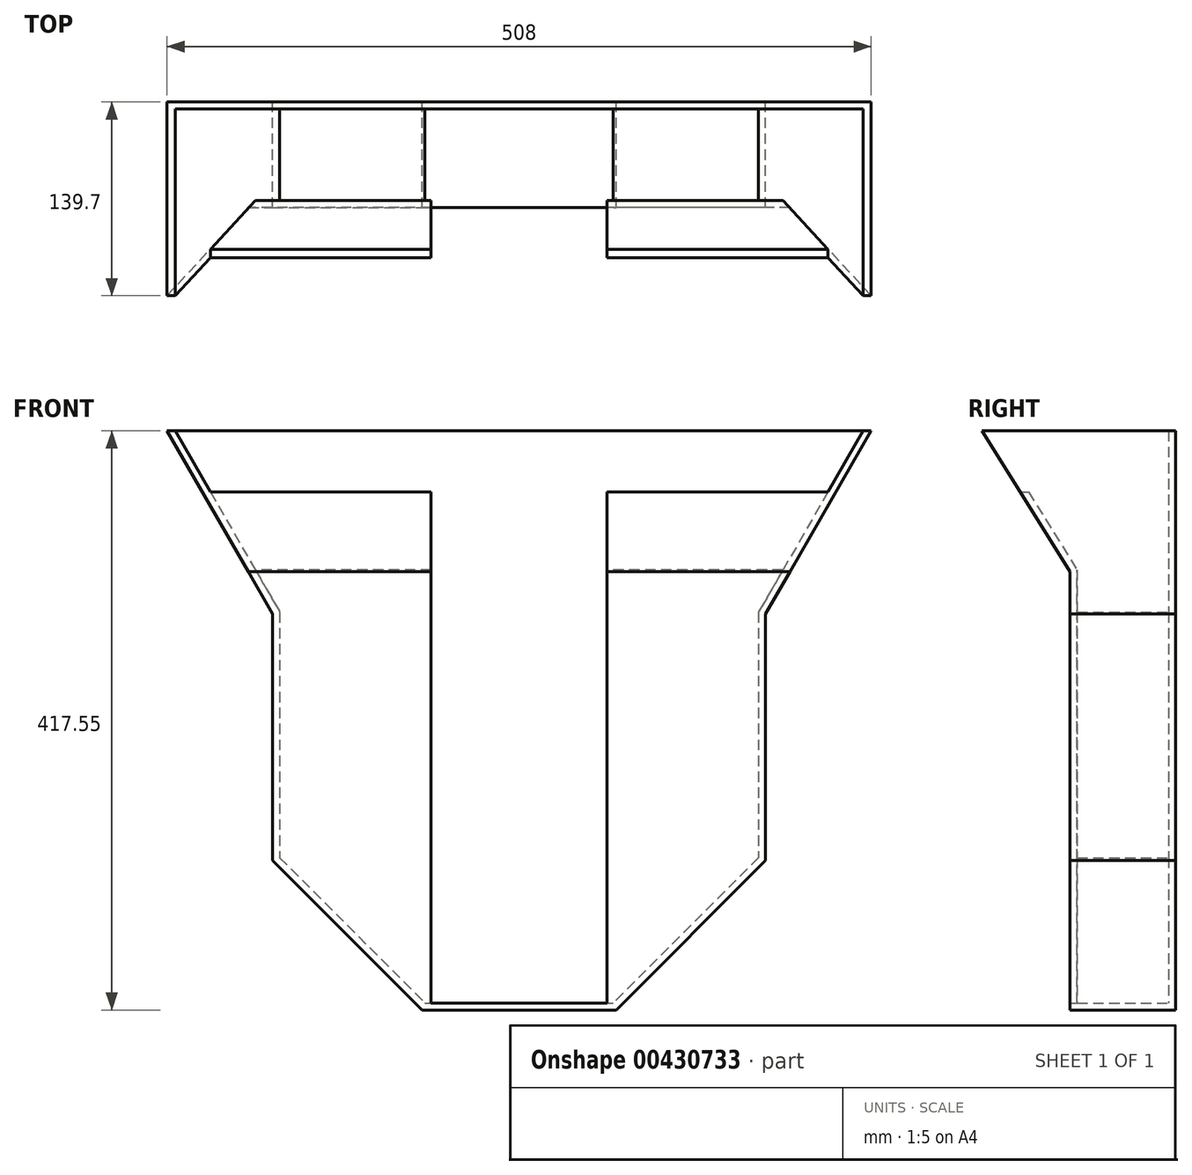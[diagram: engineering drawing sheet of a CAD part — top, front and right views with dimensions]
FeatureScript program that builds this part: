
annotation { "Feature Type Name" : "Feature", "Feature Type Description" : "" }
export const myFeature = defineFeature(function(context is Context, id is Id, definition is map)
    precondition{}
    {
        {
            var Q0;
            Q0=qCreatedBy(makeId("Front.planeOp"),FACE);
            var sketch = newSketch(context, id + "F0", { "sketchPlane" : qUnion([Q0])});
            skLineSegment(sketch, "E0", {"start": v(0, 0) * mm, "end": v(254, 0) * mm});
            skLineSegment(sketch, "E1", {"start": v(254, 0) * mm, "end": v(177.8, -131.98) * mm});
            skLineSegment(sketch, "E2", {"start": v(177.8, -131.98) * mm, "end": v(177.8, -309.78) * mm});
            skLineSegment(sketch, "E3", {"start": v(177.8, -309.78) * mm, "end": v(70.04, -417.55) * mm});
            skLineSegment(sketch, "E4", {"start": v(70.04, -417.55) * mm, "end": v(0, -417.55) * mm});
            skLineSegment(sketch, "E5.MirrorCS", {"start": v(0, 0) * mm, "end": v(-254, 0) * mm});
            skLineSegment(sketch, "E6.MirrorCS", {"start": v(-254, 0) * mm, "end": v(-177.8, -131.98) * mm});
            skLineSegment(sketch, "E7.MirrorCS", {"start": v(-177.8, -131.98) * mm, "end": v(-177.8, -309.78) * mm});
            skLineSegment(sketch, "E8.MirrorCS", {"start": v(-177.8, -309.78) * mm, "end": v(-70.04, -417.55) * mm});
            skLineSegment(sketch, "E9.MirrorCS", {"start": v(-70.04, -417.55) * mm, "end": v(0, -417.55) * mm});
            skSolve(sketch);
        }
        {
            var Q0;
            Q0=makeQuery(id+"F0.imprint","IMPRINT",FACE,{"disambiguationData":[TD([[makeQuery(id+"F0.imprint","IMPRINT",EDGE,{"derivedFrom":sQuery(id+"F0.wireOp",EDGE,"E0")}),-1.0]])]});
            extrude(context, id + "F1", {"entities" : qUnion([Q0]), "depth" : 76.2 * mm});
        }
        {
            var Q0;
            Q0=qCreatedBy(makeId("Right.planeOp"),FACE);
            var sketch = newSketch(context, id + "F2", { "sketchPlane" : qUnion([Q0])});
            skLineSegment(sketch, "E10", {"start": v(-76.2, 0) * mm, "end": v(-139.7, 0) * mm});
            skLineSegment(sketch, "E11", {"start": v(-139.7, 0) * mm, "end": v(-76.2, -101.6) * mm});
            skLineSegment(sketch, "E12", {"start": v(-76.2, -101.6) * mm, "end": v(-76.2, 0) * mm});
            skSolve(sketch);
        }
        {
            var Q0;
            Q0 = qSketchRegion(id + "F2", true);
            var Q1;
            Q1=makeQuery(id+"F1.opExtrude","SWEPT_FACE",FACE,{"disambiguationData":[OSD([sQuery(id+"F0.wireOp",EDGE,"E1")])]});
            var Q2;
            Q2=makeQuery(id+"F1.opExtrude","SWEPT_FACE",FACE,{"disambiguationData":[OSD([sQuery(id+"F0.wireOp",EDGE,"E6.MirrorCS")])]});
            extrude(context, id + "F3", {"entities" : qUnion([Q0]), "operationType" : NewBodyOperationType.ADD, "endBound" : BoundingType.UP_TO_SURFACE, "endBoundEntityFace" : qUnion([Q1]), "depth" : 25.4 * mm, "hasSecondDirection" : true, "secondDirectionBound" : BoundingType.UP_TO_SURFACE, "secondDirectionOppositeDirection" : true, "secondDirectionBoundEntityFace" : qUnion([Q2]), "secondDirectionDepth" : 25.4 * mm});
        }
        {
            var Q0;
            Q0=makeQuery(id+"F3.boolean.opBoolean","MERGE",FACE,{"derivedFrom":[makeQuery(id+"F1.opExtrude","SWEPT_FACE",FACE,{"disambiguationData":[OSD([sQuery(id+"F0.wireOp",EDGE,"E0"),sQuery(id+"F0.wireOp",EDGE,"E5.MirrorCS")])]}),makeQuery(id+"F3.opExtrude","SWEPT_FACE",FACE,{"disambiguationData":[OSD([sQuery(id+"F2.wireOp",EDGE,"E10")])]})]});
            shell(context, id + "F4", {"entities" : qUnion([Q0]), "thickness" : 5.08 * mm});
        }
        {
            var Q0;
            {var subQ0=sQuery(id+"F0.wireOp",EDGE,"E9.MirrorCS");var subQ1=sQuery(id+"F0.wireOp",EDGE,"E8.MirrorCS");var subQ2=sQuery(id+"F0.wireOp",EDGE,"E7.MirrorCS");var subQ3=sQuery(id+"F0.wireOp",EDGE,"E6.MirrorCS");var subQ4=sQuery(id+"F0.wireOp",EDGE,"E5.MirrorCS");var subQ5=sQuery(id+"F0.wireOp",EDGE,"E4");var subQ6=sQuery(id+"F0.wireOp",EDGE,"E3");var subQ7=sQuery(id+"F0.wireOp",EDGE,"E2");var subQ8=sQuery(id+"F0.wireOp",EDGE,"E1");var subQ9=sQuery(id+"F0.wireOp",EDGE,"E0");Q0=makeQuery(id+"F4.opShell","OFFSET_FACE",FACE,{"disambiguationData":[OSD([subQ9,subQ8,subQ7,subQ6,subQ5,subQ4,subQ3,subQ2,subQ1,subQ0]),TDD([makeQuery(id+"F1.opExtrude","CAP_FACE",FACE,{"disambiguationData":[OSD([subQ9,subQ8,subQ7,subQ6,subQ5,subQ4,subQ3,subQ2,subQ1,subQ0])],"isStart":true})])]});}
            var sketch = newSketch(context, id + "F5", { "sketchPlane" : qUnion([Q0])});
            skLineSegment(sketch, "E13.bottom", {"start": v(63.5, 0) * mm, "end": v(-63.5, 0) * mm});
            skLineSegment(sketch, "E13.top", {"start": v(63.5, -412.47) * mm, "end": v(-63.5, -412.47) * mm});
            skLineSegment(sketch, "E13.left", {"start": v(63.5, 0) * mm, "end": v(63.5, -412.47) * mm});
            skLineSegment(sketch, "E13.right", {"start": v(-63.5, 0) * mm, "end": v(-63.5, -412.47) * mm});
            skLineSegment(sketch, "E14", {"start": v(-248.13, 0) * mm, "end": v(-222.73, -44) * mm});
            skLineSegment(sketch, "E15", {"start": v(222.73, -44) * mm, "end": v(248.13, 0) * mm});
            skLineSegment(sketch, "E16", {"start": v(248.13, 0) * mm, "end": v(-248.13, 0) * mm});
            skLineSegment(sketch, "E17", {"start": v(-222.73, -44) * mm, "end": v(222.73, -44) * mm});
            skPoint(sketch, "E18.orphan", {"position": v(-210.43, -65.31) * mm});
            skPoint(sketch, "E19.orphan", {"position": v(210.43, -65.31) * mm});
            skSolve(sketch);
        }
        {
            var Q0;
            Q0=makeQuery(id+"F5.imprint","IMPRINT",FACE,{"disambiguationData":[TD([[makeQuery(id+"F5.imprint","IMPRINT",EDGE,{"derivedFrom":sQuery(id+"F5.wireOp",EDGE,"E13.bottom")}),-1.0]])]});
            var Q1;
            {var subQ0=sQuery(id+"F5.wireOp",EDGE,"E16");var subQ1=sQuery(id+"F5.wireOp",EDGE,"E13.left");var subQ2=makeQuery(id+"F5.imprint","INTERSECT",VERTEX,{"derivedFrom":[subQ1,subQ0]});Q1=makeQuery(id+"F5.imprint","IMPRINT",FACE,{"disambiguationData":[TD([[makeQuery(id+"F5.imprint","IMPRINT",EDGE,{"disambiguationData":[TD([[subQ2,-1.0]])],"derivedFrom":subQ1}),-1.0]])]});}
            var Q2;
            {var subQ5=sQuery(id+"F5.wireOp",EDGE,"E14");Q2=makeQuery(id+"F5.imprint","IMPRINT",FACE,{"disambiguationData":[TD([[makeQuery(id+"F5.imprint","IMPRINT",EDGE,{"derivedFrom":subQ5}),1.0]])]});}
            var Q3;
            {var subQ5=sQuery(id+"F5.wireOp",EDGE,"E15");Q3=makeQuery(id+"F5.imprint","IMPRINT",FACE,{"disambiguationData":[TD([[makeQuery(id+"F5.imprint","IMPRINT",EDGE,{"derivedFrom":subQ5}),-1.0]])]});}
            var Q4;
            Q4=makeQuery(id+"F1.opExtrude","CAP_FACE",FACE,{"disambiguationData":[OSD([sQuery(id+"F0.wireOp",EDGE,"E0"),sQuery(id+"F0.wireOp",EDGE,"E1"),sQuery(id+"F0.wireOp",EDGE,"E2"),sQuery(id+"F0.wireOp",EDGE,"E3"),sQuery(id+"F0.wireOp",EDGE,"E4"),sQuery(id+"F0.wireOp",EDGE,"E5.MirrorCS"),sQuery(id+"F0.wireOp",EDGE,"E6.MirrorCS"),sQuery(id+"F0.wireOp",EDGE,"E7.MirrorCS"),sQuery(id+"F0.wireOp",EDGE,"E8.MirrorCS"),sQuery(id+"F0.wireOp",EDGE,"E9.MirrorCS")])],"isStart":false});
            var Q5;
            {var subQ0=sQuery(id+"F5.wireOp",EDGE,"E13.top");Q5=makeQuery(id+"F5.imprint","IMPRINT",FACE,{"disambiguationData":[TD([[makeQuery(id+"F5.imprint","IMPRINT",EDGE,{"derivedFrom":subQ0}),1.0]])]});}
            extrude(context, id + "F6", {"entities" : qUnion([Q0, Q1, Q2, Q3, Q4, Q5]), "operationType" : NewBodyOperationType.REMOVE, "endBound" : BoundingType.THROUGH_ALL, "depth" : 25.4 * mm});
        }
    });
